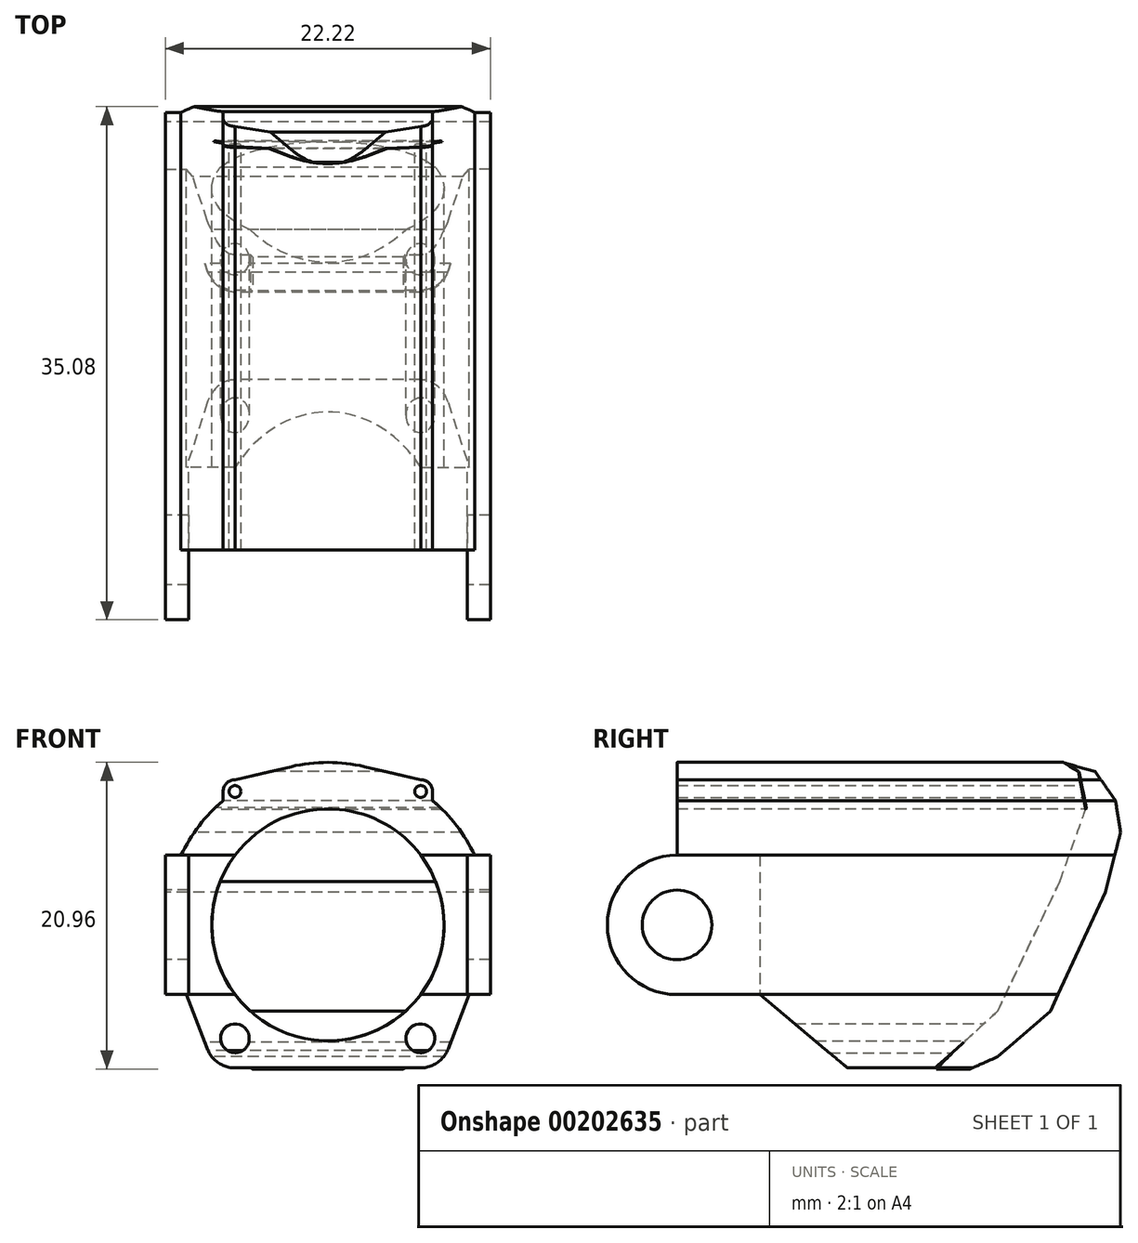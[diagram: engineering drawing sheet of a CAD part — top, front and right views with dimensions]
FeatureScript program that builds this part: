
annotation { "Feature Type Name" : "Feature", "Feature Type Description" : "" }
export const myFeature = defineFeature(function(context is Context, id is Id, definition is map)
    precondition{}
    {
        {
            var Q0;
            Q0=qCreatedBy(makeId("Front.planeOp"),FACE);
            var sketch = newSketch(context, id + "F0", { "sketchPlane" : qUnion([Q0])});
            skCircle(sketch, "E0", {"center": v(-21.38, 17.33) * mm, "radius": 7.94 * mm});
            skCircle(sketch, "E1", {"center": v(-21.38, 17.33) * mm, "radius": 9.53 * mm});
            skCircle(sketch, "E2", {"center": v(-21.38, 17.33) * mm, "radius": 11.11 * mm});
            skLineSegment(sketch, "E3", {"start": v(-33.5, 17.33) * mm, "end": v(-8.67, 17.33) * mm});
            skLineSegment(sketch, "E4", {"start": v(-21.38, 30.04) * mm, "end": v(-21.38, 4.75) * mm, "construction": true});
            skArc(sketch, "E5", {"start": v(-32.5, 17.33) * mm, "mid": v(-28.83, 10.36) * mm, "end": v(-21.38, 7.8) * mm});
            skArc(sketch, "E6", {"start": v(-21.38, 7.8) * mm, "mid": v(-13.93, 10.36) * mm, "end": v(-10.27, 17.33) * mm});
            skLineSegment(sketch, "E7", {"start": v(-31.3, 7.8) * mm, "end": v(-11.33, 7.78) * mm, "construction": true});
            skLineSegment(sketch, "E8", {"start": v(-31.32, 9.58) * mm, "end": v(-11.4, 9.58) * mm, "construction": true});
            skLineSegment(sketch, "E9", {"start": v(-27.73, 6.37) * mm, "end": v(-27.73, 30.2) * mm, "construction": true});
            skLineSegment(sketch, "E10", {"start": v(-15.06, 6.13) * mm, "end": v(-15.03, 30.29) * mm, "construction": true});
            skCircle(sketch, "E11", {"center": v(-15.06, 9.58) * mm, "radius": 1 * mm});
            skCircle(sketch, "E12", {"center": v(-15.06, 9.58) * mm, "radius": 2.03 * mm});
            skCircle(sketch, "E13", {"center": v(-27.73, 9.58) * mm, "radius": 1 * mm});
            skCircle(sketch, "E14", {"center": v(-27.73, 9.58) * mm, "radius": 2.03 * mm});
            skLineSegment(sketch, "E15", {"start": v(-31.83, 14.6) * mm, "end": v(-29.63, 8.85) * mm});
            skLineSegment(sketch, "E16", {"start": v(-10.98, 14.49) * mm, "end": v(-13.16, 8.85) * mm});
            skLineSegment(sketch, "E17", {"start": v(-27.73, 7.55) * mm, "end": v(-15.06, 7.55) * mm});
            skCircle(sketch, "E18", {"center": v(-15.04, 26.45) * mm, "radius": 0.4 * mm});
            skCircle(sketch, "E19", {"center": v(-27.73, 26.45) * mm, "radius": 0.4 * mm});
            skCircle(sketch, "E20", {"center": v(-27.73, 26.45) * mm, "radius": 0.81 * mm});
            skCircle(sketch, "E21", {"center": v(-15.04, 26.45) * mm, "radius": 0.81 * mm});
            skLineSegment(sketch, "E22", {"start": v(-27.73, 27.26) * mm, "end": v(-23.9, 28.15) * mm});
            skLineSegment(sketch, "E23", {"start": v(-15.03, 27.26) * mm, "end": v(-18.87, 28.15) * mm});
            skLineSegment(sketch, "E24", {"start": v(-15.54, 26.45) * mm, "end": v(-13.99, 26.45) * mm, "construction": true});
            skLineSegment(sketch, "E25", {"start": v(-27.17, 26.45) * mm, "end": v(-28.9, 26.45) * mm, "construction": true});
            skLineSegment(sketch, "E26", {"start": v(-28.54, 26.45) * mm, "end": v(-28.54, 25.82) * mm});
            skLineSegment(sketch, "E27", {"start": v(-14.22, 26.45) * mm, "end": v(-14.22, 25.83) * mm});
            skLineSegment(sketch, "E28", {"start": v(-13.44, 17.33) * mm, "end": v(-13.44, 28.69) * mm, "construction": true});
            skLineSegment(sketch, "E29", {"start": v(-29.32, 17.33) * mm, "end": v(-29.32, 27.77) * mm, "construction": true});
            skLineSegment(sketch, "E30.bottom", {"start": v(-13.44, 22.1) * mm, "end": v(-10.27, 22.1) * mm});
            skLineSegment(sketch, "E30.top", {"start": v(-13.44, 12.57) * mm, "end": v(-10.27, 12.57) * mm});
            skLineSegment(sketch, "E30.left", {"start": v(-13.44, 22.1) * mm, "end": v(-13.44, 12.57) * mm});
            skLineSegment(sketch, "E30.right", {"start": v(-10.27, 22.1) * mm, "end": v(-10.27, 12.57) * mm});
            skLineSegment(sketch, "E31.bottom", {"start": v(-29.32, 22.1) * mm, "end": v(-32.5, 22.1) * mm});
            skLineSegment(sketch, "E31.top", {"start": v(-29.32, 12.57) * mm, "end": v(-32.5, 12.57) * mm});
            skLineSegment(sketch, "E31.left", {"start": v(-29.32, 22.1) * mm, "end": v(-29.32, 12.57) * mm});
            skLineSegment(sketch, "E31.right", {"start": v(-32.5, 22.1) * mm, "end": v(-32.5, 12.57) * mm});
            skSolve(sketch);
        }
        {
            var Q0;
            {var subQ4=sQuery(id+"F0.wireOp",EDGE,"E30.bottom");var subQ6=sQuery(id+"F0.wireOp",EDGE,"E1");var subQ7=makeQuery(id+"F0.imprint","INTERSECT",VERTEX,{"derivedFrom":[subQ6,subQ4]});Q0=makeQuery(id+"F0.imprint","IMPRINT",FACE,{"disambiguationData":[TD([[makeQuery(id+"F0.imprint","IMPRINT",EDGE,{"disambiguationData":[TD([[subQ7,-1.0]])],"derivedFrom":subQ6}),-1.0]])]});}
            var Q1;
            {var subQ1=sQuery(id+"F0.wireOp",EDGE,"E30.bottom");var subQ9=sQuery(id+"F0.wireOp",EDGE,"E1");var subQ11=makeQuery(id+"F0.imprint","INTERSECT",VERTEX,{"derivedFrom":[subQ9,subQ1]});Q1=makeQuery(id+"F0.imprint","IMPRINT",FACE,{"disambiguationData":[TD([[makeQuery(id+"F0.imprint","IMPRINT",EDGE,{"disambiguationData":[TD([[subQ11,-1.0]])],"derivedFrom":subQ9}),1.0]])]});}
            var Q2;
            {var subQ0=sQuery(id+"F0.wireOp",EDGE,"E22");Q2=makeQuery(id+"F0.imprint","IMPRINT",FACE,{"disambiguationData":[TD([[makeQuery(id+"F0.imprint","IMPRINT",EDGE,{"derivedFrom":subQ0}),-1.0]])]});}
            var Q3;
            {var subQ0=sQuery(id+"F0.wireOp",EDGE,"E20");var subQ2=sQuery(id+"F0.wireOp",EDGE,"E2");var subQ3=makeQuery(id+"F0.imprint","INTERSECT",VERTEX,{"disambiguationData":[OD(0.0)],"derivedFrom":[subQ2,subQ0]});Q3=makeQuery(id+"F0.imprint","IMPRINT",FACE,{"disambiguationData":[TD([[makeQuery(id+"F0.imprint","IMPRINT",EDGE,{"disambiguationData":[TD([[subQ3,-1.0]])],"derivedFrom":subQ2}),-1.0]])]});}
            var Q4;
            {var subQ0=sQuery(id+"F0.wireOp",EDGE,"E20");var subQ1=sQuery(id+"F0.wireOp",EDGE,"E2");var subQ2=makeQuery(id+"F0.imprint","INTERSECT",VERTEX,{"disambiguationData":[OD(0.0)],"derivedFrom":[subQ1,subQ0]});Q4=makeQuery(id+"F0.imprint","IMPRINT",FACE,{"disambiguationData":[TD([[makeQuery(id+"F0.imprint","IMPRINT",EDGE,{"disambiguationData":[TD([[subQ2,-1.0]])],"derivedFrom":subQ1}),1.0]])]});}
            var Q5;
            {var subQ0=sQuery(id+"F0.wireOp",EDGE,"E26");Q5=makeQuery(id+"F0.imprint","IMPRINT",FACE,{"disambiguationData":[TD([[makeQuery(id+"F0.imprint","IMPRINT",EDGE,{"derivedFrom":subQ0}),1.0]])]});}
            var Q6;
            {var subQ0=sQuery(id+"F0.wireOp",EDGE,"E31.bottom");var subQ1=sQuery(id+"F0.wireOp",EDGE,"E1");var subQ2=makeQuery(id+"F0.imprint","INTERSECT",VERTEX,{"derivedFrom":[subQ1,subQ0]});Q6=makeQuery(id+"F0.imprint","IMPRINT",FACE,{"disambiguationData":[TD([[makeQuery(id+"F0.imprint","IMPRINT",EDGE,{"disambiguationData":[TD([[subQ2,-1.0]])],"derivedFrom":subQ1}),1.0]])]});}
            var Q7;
            {var subQ0=sQuery(id+"F0.wireOp",EDGE,"E31.bottom");var subQ1=sQuery(id+"F0.wireOp",EDGE,"E1");var subQ2=makeQuery(id+"F0.imprint","INTERSECT",VERTEX,{"derivedFrom":[subQ1,subQ0]});Q7=makeQuery(id+"F0.imprint","IMPRINT",FACE,{"disambiguationData":[TD([[makeQuery(id+"F0.imprint","IMPRINT",EDGE,{"disambiguationData":[TD([[subQ2,-1.0]])],"derivedFrom":subQ1}),-1.0]])]});}
            var Q8;
            {var subQ0=sQuery(id+"F0.wireOp",EDGE,"E31.right");var subQ3=sQuery(id+"F0.wireOp",EDGE,"E31.bottom");var subQ5=makeQuery(id+"F0.imprint","INTERSECT",VERTEX,{"derivedFrom":[subQ3,subQ0]});Q8=makeQuery(id+"F0.imprint","IMPRINT",FACE,{"disambiguationData":[TD([[makeQuery(id+"F0.imprint","IMPRINT",EDGE,{"disambiguationData":[TD([[subQ5,1.0]])],"derivedFrom":subQ3}),1.0]])]});}
            var Q9;
            {var subQ0=sQuery(id+"F0.wireOp",EDGE,"E3");var subQ1=sQuery(id+"F0.wireOp",EDGE,"E1");var subQ2=makeQuery(id+"F0.imprint","INTERSECT",VERTEX,{"disambiguationData":[OD(1.0)],"derivedFrom":[subQ1,subQ0]});Q9=makeQuery(id+"F0.imprint","IMPRINT",FACE,{"disambiguationData":[TD([[makeQuery(id+"F0.imprint","IMPRINT",EDGE,{"disambiguationData":[TD([[subQ2,-1.0]])],"derivedFrom":subQ1}),1.0]])]});}
            var Q10;
            {var subQ1=sQuery(id+"F0.wireOp",EDGE,"E3");var subQ4=sQuery(id+"F0.wireOp",EDGE,"E1");var subQ5=makeQuery(id+"F0.imprint","INTERSECT",VERTEX,{"disambiguationData":[OD(1.0)],"derivedFrom":[subQ4,subQ1]});Q10=makeQuery(id+"F0.imprint","IMPRINT",FACE,{"disambiguationData":[TD([[makeQuery(id+"F0.imprint","IMPRINT",EDGE,{"disambiguationData":[TD([[subQ5,-1.0]])],"derivedFrom":subQ4}),-1.0]])]});}
            var Q11;
            {var subQ0=sQuery(id+"F0.wireOp",EDGE,"E31.right");var subQ3=sQuery(id+"F0.wireOp",EDGE,"E31.top");var subQ5=makeQuery(id+"F0.imprint","INTERSECT",VERTEX,{"derivedFrom":[subQ3,subQ0]});Q11=makeQuery(id+"F0.imprint","IMPRINT",FACE,{"disambiguationData":[TD([[makeQuery(id+"F0.imprint","IMPRINT",EDGE,{"disambiguationData":[TD([[subQ5,1.0]])],"derivedFrom":subQ3}),-1.0]])]});}
            var Q12;
            {var subQ0=sQuery(id+"F0.wireOp",EDGE,"E5");var subQ5=sQuery(id+"F0.wireOp",EDGE,"E15");var subQ6=makeQuery(id+"F0.imprint","INTERSECT",VERTEX,{"derivedFrom":[subQ0,subQ5]});Q12=makeQuery(id+"F0.imprint","IMPRINT",FACE,{"disambiguationData":[TD([[makeQuery(id+"F0.imprint","IMPRINT",EDGE,{"disambiguationData":[TD([[subQ6,-1.0]])],"derivedFrom":subQ5}),-1.0]])]});}
            var Q13;
            {var subQ0=sQuery(id+"F0.wireOp",EDGE,"E15");var subQ1=sQuery(id+"F0.wireOp",EDGE,"E5");var subQ2=makeQuery(id+"F0.imprint","INTERSECT",VERTEX,{"derivedFrom":[subQ1,subQ0]});Q13=makeQuery(id+"F0.imprint","IMPRINT",FACE,{"disambiguationData":[TD([[makeQuery(id+"F0.imprint","IMPRINT",EDGE,{"disambiguationData":[TD([[subQ2,-1.0]])],"derivedFrom":subQ1}),-1.0]])]});}
            var Q14;
            {var subQ1=sQuery(id+"F0.wireOp",EDGE,"E31.top");var subQ3=sQuery(id+"F0.wireOp",EDGE,"E1");var subQ4=makeQuery(id+"F0.imprint","INTERSECT",VERTEX,{"derivedFrom":[subQ3,subQ1]});Q14=makeQuery(id+"F0.imprint","IMPRINT",FACE,{"disambiguationData":[TD([[makeQuery(id+"F0.imprint","IMPRINT",EDGE,{"disambiguationData":[TD([[subQ4,-1.0]])],"derivedFrom":subQ3}),1.0]])]});}
            var Q15;
            {var subQ1=sQuery(id+"F0.wireOp",EDGE,"E2");var subQ5=sQuery(id+"F0.wireOp",EDGE,"E15");var subQ6=makeQuery(id+"F0.imprint","INTERSECT",VERTEX,{"derivedFrom":[subQ1,subQ5]});Q15=makeQuery(id+"F0.imprint","IMPRINT",FACE,{"disambiguationData":[TD([[makeQuery(id+"F0.imprint","IMPRINT",EDGE,{"disambiguationData":[TD([[subQ6,-1.0]])],"derivedFrom":subQ1}),1.0]])]});}
            var Q16;
            {var subQ0=sQuery(id+"F0.wireOp",EDGE,"E31.top");var subQ1=sQuery(id+"F0.wireOp",EDGE,"E1");var subQ2=makeQuery(id+"F0.imprint","INTERSECT",VERTEX,{"derivedFrom":[subQ1,subQ0]});Q16=makeQuery(id+"F0.imprint","IMPRINT",FACE,{"disambiguationData":[TD([[makeQuery(id+"F0.imprint","IMPRINT",EDGE,{"disambiguationData":[TD([[subQ2,-1.0]])],"derivedFrom":subQ1}),-1.0]])]});}
            var Q17;
            {var subQ0=sQuery(id+"F0.wireOp",EDGE,"E14");var subQ1=sQuery(id+"F0.wireOp",EDGE,"E1");var subQ2=makeQuery(id+"F0.imprint","INTERSECT",VERTEX,{"disambiguationData":[OD(0.0)],"derivedFrom":[subQ1,subQ0]});Q17=makeQuery(id+"F0.imprint","IMPRINT",FACE,{"disambiguationData":[TD([[makeQuery(id+"F0.imprint","IMPRINT",EDGE,{"disambiguationData":[TD([[subQ2,-1.0]])],"derivedFrom":subQ1}),1.0]])]});}
            var Q18;
            {var subQ0=sQuery(id+"F0.wireOp",EDGE,"E14");var subQ1=sQuery(id+"F0.wireOp",EDGE,"E1");var subQ2=makeQuery(id+"F0.imprint","INTERSECT",VERTEX,{"disambiguationData":[OD(0.0)],"derivedFrom":[subQ1,subQ0]});Q18=makeQuery(id+"F0.imprint","IMPRINT",FACE,{"disambiguationData":[TD([[makeQuery(id+"F0.imprint","IMPRINT",EDGE,{"disambiguationData":[TD([[subQ2,-1.0]])],"derivedFrom":subQ1}),-1.0]])]});}
            var Q19;
            {var subQ4=sQuery(id+"F0.wireOp",EDGE,"E14");var subQ7=sQuery(id+"F0.wireOp",EDGE,"E2");var subQ9=makeQuery(id+"F0.imprint","INTERSECT",VERTEX,{"disambiguationData":[OD(0.0)],"derivedFrom":[subQ7,subQ4]});Q19=makeQuery(id+"F0.imprint","IMPRINT",FACE,{"disambiguationData":[TD([[makeQuery(id+"F0.imprint","IMPRINT",EDGE,{"disambiguationData":[TD([[subQ9,-1.0]])],"derivedFrom":subQ7}),1.0]])]});}
            var Q20;
            {var subQ0=sQuery(id+"F0.wireOp",EDGE,"E13");var subQ1=sQuery(id+"F0.wireOp",EDGE,"E1");var subQ2=makeQuery(id+"F0.imprint","INTERSECT",VERTEX,{"disambiguationData":[OD(1.0)],"derivedFrom":[subQ1,subQ0]});Q20=makeQuery(id+"F0.imprint","IMPRINT",FACE,{"disambiguationData":[TD([[makeQuery(id+"F0.imprint","IMPRINT",EDGE,{"disambiguationData":[TD([[subQ2,-1.0]])],"derivedFrom":subQ1}),-1.0]])]});}
            var Q21;
            {var subQ0=sQuery(id+"F0.wireOp",EDGE,"E14");var subQ1=sQuery(id+"F0.wireOp",EDGE,"E2");var subQ2=makeQuery(id+"F0.imprint","INTERSECT",VERTEX,{"disambiguationData":[OD(0.0)],"derivedFrom":[subQ1,subQ0]});Q21=makeQuery(id+"F0.imprint","IMPRINT",FACE,{"disambiguationData":[TD([[makeQuery(id+"F0.imprint","IMPRINT",EDGE,{"disambiguationData":[TD([[subQ2,-1.0]])],"derivedFrom":subQ1}),-1.0]])]});}
            var Q22;
            {var subQ0=sQuery(id+"F0.wireOp",EDGE,"E15");var subQ1=sQuery(id+"F0.wireOp",EDGE,"E2");var subQ2=makeQuery(id+"F0.imprint","INTERSECT",VERTEX,{"derivedFrom":[subQ1,subQ0]});Q22=makeQuery(id+"F0.imprint","IMPRINT",FACE,{"disambiguationData":[TD([[makeQuery(id+"F0.imprint","IMPRINT",EDGE,{"disambiguationData":[TD([[subQ2,-1.0]])],"derivedFrom":subQ1}),-1.0]])]});}
            var Q23;
            {var subQ1=sQuery(id+"F0.wireOp",EDGE,"E1");var subQ3=sQuery(id+"F0.wireOp",EDGE,"E14");var subQ4=makeQuery(id+"F0.imprint","INTERSECT",VERTEX,{"disambiguationData":[OD(1.0)],"derivedFrom":[subQ1,subQ3]});Q23=makeQuery(id+"F0.imprint","IMPRINT",FACE,{"disambiguationData":[TD([[makeQuery(id+"F0.imprint","IMPRINT",EDGE,{"disambiguationData":[TD([[subQ4,1.0]])],"derivedFrom":subQ3}),-1.0]])]});}
            var Q24;
            {var subQ7=sQuery(id+"F0.wireOp",EDGE,"E17");var subQ8=sQuery(id+"F0.wireOp",EDGE,"E2");var subQ11=makeQuery(id+"F0.imprint","INTERSECT",VERTEX,{"disambiguationData":[OD(0.0)],"derivedFrom":[subQ8,subQ7]});Q24=makeQuery(id+"F0.imprint","IMPRINT",FACE,{"disambiguationData":[TD([[makeQuery(id+"F0.imprint","IMPRINT",EDGE,{"disambiguationData":[TD([[subQ11,1.0]])],"derivedFrom":subQ8}),1.0]])]});}
            var Q25;
            {var subQ0=sQuery(id+"F0.wireOp",EDGE,"E17");var subQ1=sQuery(id+"F0.wireOp",EDGE,"E2");var subQ2=makeQuery(id+"F0.imprint","INTERSECT",VERTEX,{"disambiguationData":[OD(0.0)],"derivedFrom":[subQ1,subQ0]});Q25=makeQuery(id+"F0.imprint","IMPRINT",FACE,{"disambiguationData":[TD([[makeQuery(id+"F0.imprint","IMPRINT",EDGE,{"disambiguationData":[TD([[subQ2,1.0]])],"derivedFrom":subQ1}),-1.0]])]});}
            var Q26;
            {var subQ1=sQuery(id+"F0.wireOp",EDGE,"E1");var subQ3=sQuery(id+"F0.wireOp",EDGE,"E12");var subQ4=makeQuery(id+"F0.imprint","INTERSECT",VERTEX,{"disambiguationData":[OD(0.0)],"derivedFrom":[subQ1,subQ3]});Q26=makeQuery(id+"F0.imprint","IMPRINT",FACE,{"disambiguationData":[TD([[makeQuery(id+"F0.imprint","IMPRINT",EDGE,{"disambiguationData":[TD([[subQ4,-1.0]])],"derivedFrom":subQ3}),-1.0]])]});}
            var Q27;
            {var subQ0=sQuery(id+"F0.wireOp",EDGE,"E12");var subQ1=sQuery(id+"F0.wireOp",EDGE,"E1");var subQ2=makeQuery(id+"F0.imprint","INTERSECT",VERTEX,{"disambiguationData":[OD(0.0)],"derivedFrom":[subQ1,subQ0]});Q27=makeQuery(id+"F0.imprint","IMPRINT",FACE,{"disambiguationData":[TD([[makeQuery(id+"F0.imprint","IMPRINT",EDGE,{"disambiguationData":[TD([[subQ2,-1.0]])],"derivedFrom":subQ1}),1.0]])]});}
            var Q28;
            {var subQ0=sQuery(id+"F0.wireOp",EDGE,"E12");var subQ1=sQuery(id+"F0.wireOp",EDGE,"E1");var subQ2=makeQuery(id+"F0.imprint","INTERSECT",VERTEX,{"disambiguationData":[OD(0.0)],"derivedFrom":[subQ1,subQ0]});Q28=makeQuery(id+"F0.imprint","IMPRINT",FACE,{"disambiguationData":[TD([[makeQuery(id+"F0.imprint","IMPRINT",EDGE,{"disambiguationData":[TD([[subQ2,-1.0]])],"derivedFrom":subQ1}),-1.0]])]});}
            var Q29;
            {var subQ4=sQuery(id+"F0.wireOp",EDGE,"E12");var subQ7=sQuery(id+"F0.wireOp",EDGE,"E2");var subQ8=makeQuery(id+"F0.imprint","INTERSECT",VERTEX,{"disambiguationData":[OD(0.0)],"derivedFrom":[subQ7,subQ4]});Q29=makeQuery(id+"F0.imprint","IMPRINT",FACE,{"disambiguationData":[TD([[makeQuery(id+"F0.imprint","IMPRINT",EDGE,{"disambiguationData":[TD([[subQ8,-1.0]])],"derivedFrom":subQ7}),1.0]])]});}
            var Q30;
            {var subQ0=sQuery(id+"F0.wireOp",EDGE,"E17");var subQ1=sQuery(id+"F0.wireOp",EDGE,"E2");var subQ2=makeQuery(id+"F0.imprint","INTERSECT",VERTEX,{"disambiguationData":[OD(1.0)],"derivedFrom":[subQ1,subQ0]});Q30=makeQuery(id+"F0.imprint","IMPRINT",FACE,{"disambiguationData":[TD([[makeQuery(id+"F0.imprint","IMPRINT",EDGE,{"disambiguationData":[TD([[subQ2,-1.0]])],"derivedFrom":subQ1}),-1.0]])]});}
            var Q31;
            {var subQ0=sQuery(id+"F0.wireOp",EDGE,"E12");var subQ1=sQuery(id+"F0.wireOp",EDGE,"E2");var subQ2=makeQuery(id+"F0.imprint","INTERSECT",VERTEX,{"disambiguationData":[OD(0.0)],"derivedFrom":[subQ1,subQ0]});Q31=makeQuery(id+"F0.imprint","IMPRINT",FACE,{"disambiguationData":[TD([[makeQuery(id+"F0.imprint","IMPRINT",EDGE,{"disambiguationData":[TD([[subQ2,-1.0]])],"derivedFrom":subQ1}),-1.0]])]});}
            var Q32;
            {var subQ0=sQuery(id+"F0.wireOp",EDGE,"E16");var subQ1=sQuery(id+"F0.wireOp",EDGE,"E2");var subQ2=makeQuery(id+"F0.imprint","INTERSECT",VERTEX,{"derivedFrom":[subQ1,subQ0]});Q32=makeQuery(id+"F0.imprint","IMPRINT",FACE,{"disambiguationData":[TD([[makeQuery(id+"F0.imprint","IMPRINT",EDGE,{"disambiguationData":[TD([[subQ2,1.0]])],"derivedFrom":subQ1}),-1.0]])]});}
            var Q33;
            {var subQ1=sQuery(id+"F0.wireOp",EDGE,"E2");var subQ5=sQuery(id+"F0.wireOp",EDGE,"E16");var subQ6=makeQuery(id+"F0.imprint","INTERSECT",VERTEX,{"derivedFrom":[subQ1,subQ5]});Q33=makeQuery(id+"F0.imprint","IMPRINT",FACE,{"disambiguationData":[TD([[makeQuery(id+"F0.imprint","IMPRINT",EDGE,{"disambiguationData":[TD([[subQ6,1.0]])],"derivedFrom":subQ1}),1.0]])]});}
            var Q34;
            {var subQ0=sQuery(id+"F0.wireOp",EDGE,"E12");var subQ1=sQuery(id+"F0.wireOp",EDGE,"E1");var subQ2=makeQuery(id+"F0.imprint","INTERSECT",VERTEX,{"disambiguationData":[OD(1.0)],"derivedFrom":[subQ1,subQ0]});Q34=makeQuery(id+"F0.imprint","IMPRINT",FACE,{"disambiguationData":[TD([[makeQuery(id+"F0.imprint","IMPRINT",EDGE,{"disambiguationData":[TD([[subQ2,-1.0]])],"derivedFrom":subQ1}),-1.0]])]});}
            var Q35;
            {var subQ0=sQuery(id+"F0.wireOp",EDGE,"E11");var subQ1=sQuery(id+"F0.wireOp",EDGE,"E1");var subQ2=makeQuery(id+"F0.imprint","INTERSECT",VERTEX,{"disambiguationData":[OD(1.0)],"derivedFrom":[subQ1,subQ0]});Q35=makeQuery(id+"F0.imprint","IMPRINT",FACE,{"disambiguationData":[TD([[makeQuery(id+"F0.imprint","IMPRINT",EDGE,{"disambiguationData":[TD([[subQ2,-1.0]])],"derivedFrom":subQ1}),-1.0]])]});}
            var Q36;
            {var subQ0=sQuery(id+"F0.wireOp",EDGE,"E3");var subQ1=sQuery(id+"F0.wireOp",EDGE,"E1");var subQ2=makeQuery(id+"F0.imprint","INTERSECT",VERTEX,{"disambiguationData":[OD(0.0)],"derivedFrom":[subQ1,subQ0]});Q36=makeQuery(id+"F0.imprint","IMPRINT",FACE,{"disambiguationData":[TD([[makeQuery(id+"F0.imprint","IMPRINT",EDGE,{"disambiguationData":[TD([[subQ2,1.0]])],"derivedFrom":subQ1}),1.0]])]});}
            var Q37;
            {var subQ4=sQuery(id+"F0.wireOp",EDGE,"E3");var subQ6=sQuery(id+"F0.wireOp",EDGE,"E1");var subQ7=makeQuery(id+"F0.imprint","INTERSECT",VERTEX,{"disambiguationData":[OD(0.0)],"derivedFrom":[subQ6,subQ4]});Q37=makeQuery(id+"F0.imprint","IMPRINT",FACE,{"disambiguationData":[TD([[makeQuery(id+"F0.imprint","IMPRINT",EDGE,{"disambiguationData":[TD([[subQ7,1.0]])],"derivedFrom":subQ6}),-1.0]])]});}
            var Q38;
            {var subQ0=sQuery(id+"F0.wireOp",EDGE,"E16");var subQ1=sQuery(id+"F0.wireOp",EDGE,"E6");var subQ2=makeQuery(id+"F0.imprint","INTERSECT",VERTEX,{"derivedFrom":[subQ1,subQ0]});Q38=makeQuery(id+"F0.imprint","IMPRINT",FACE,{"disambiguationData":[TD([[makeQuery(id+"F0.imprint","IMPRINT",EDGE,{"disambiguationData":[TD([[subQ2,1.0]])],"derivedFrom":subQ1}),-1.0]])]});}
            var Q39;
            {var subQ0=sQuery(id+"F0.wireOp",EDGE,"E6");var subQ5=sQuery(id+"F0.wireOp",EDGE,"E16");var subQ6=makeQuery(id+"F0.imprint","INTERSECT",VERTEX,{"derivedFrom":[subQ0,subQ5]});Q39=makeQuery(id+"F0.imprint","IMPRINT",FACE,{"disambiguationData":[TD([[makeQuery(id+"F0.imprint","IMPRINT",EDGE,{"disambiguationData":[TD([[subQ6,-1.0]])],"derivedFrom":subQ5}),1.0]])]});}
            var Q40;
            {var subQ0=sQuery(id+"F0.wireOp",EDGE,"E30.right");var subQ3=sQuery(id+"F0.wireOp",EDGE,"E30.top");var subQ5=makeQuery(id+"F0.imprint","INTERSECT",VERTEX,{"derivedFrom":[subQ3,subQ0]});Q40=makeQuery(id+"F0.imprint","IMPRINT",FACE,{"disambiguationData":[TD([[makeQuery(id+"F0.imprint","IMPRINT",EDGE,{"disambiguationData":[TD([[subQ5,1.0]])],"derivedFrom":subQ3}),1.0]])]});}
            var Q41;
            {var subQ0=sQuery(id+"F0.wireOp",EDGE,"E30.right");var subQ3=sQuery(id+"F0.wireOp",EDGE,"E30.bottom");var subQ5=makeQuery(id+"F0.imprint","INTERSECT",VERTEX,{"derivedFrom":[subQ3,subQ0]});Q41=makeQuery(id+"F0.imprint","IMPRINT",FACE,{"disambiguationData":[TD([[makeQuery(id+"F0.imprint","IMPRINT",EDGE,{"disambiguationData":[TD([[subQ5,1.0]])],"derivedFrom":subQ3}),-1.0]])]});}
            var Q42;
            {var subQ0=sQuery(id+"F0.wireOp",EDGE,"E30.bottom");var subQ1=sQuery(id+"F0.wireOp",EDGE,"E1");var subQ2=makeQuery(id+"F0.imprint","INTERSECT",VERTEX,{"derivedFrom":[subQ1,subQ0]});Q42=makeQuery(id+"F0.imprint","IMPRINT",FACE,{"disambiguationData":[TD([[makeQuery(id+"F0.imprint","IMPRINT",EDGE,{"disambiguationData":[TD([[subQ2,1.0]])],"derivedFrom":subQ1}),-1.0]])]});}
            var Q43;
            {var subQ0=sQuery(id+"F0.wireOp",EDGE,"E30.bottom");var subQ1=sQuery(id+"F0.wireOp",EDGE,"E1");var subQ2=makeQuery(id+"F0.imprint","INTERSECT",VERTEX,{"derivedFrom":[subQ1,subQ0]});Q43=makeQuery(id+"F0.imprint","IMPRINT",FACE,{"disambiguationData":[TD([[makeQuery(id+"F0.imprint","IMPRINT",EDGE,{"disambiguationData":[TD([[subQ2,1.0]])],"derivedFrom":subQ1}),1.0]])]});}
            var Q44;
            {var subQ0=sQuery(id+"F0.wireOp",EDGE,"E23");Q44=makeQuery(id+"F0.imprint","IMPRINT",FACE,{"disambiguationData":[TD([[makeQuery(id+"F0.imprint","IMPRINT",EDGE,{"derivedFrom":subQ0}),1.0]])]});}
            var Q45;
            {var subQ0=sQuery(id+"F0.wireOp",EDGE,"E21");var subQ3=sQuery(id+"F0.wireOp",EDGE,"E2");var subQ4=makeQuery(id+"F0.imprint","INTERSECT",VERTEX,{"disambiguationData":[OD(0.0)],"derivedFrom":[subQ3,subQ0]});Q45=makeQuery(id+"F0.imprint","IMPRINT",FACE,{"disambiguationData":[TD([[makeQuery(id+"F0.imprint","IMPRINT",EDGE,{"disambiguationData":[TD([[subQ4,-1.0]])],"derivedFrom":subQ3}),-1.0]])]});}
            var Q46;
            {var subQ0=sQuery(id+"F0.wireOp",EDGE,"E21");var subQ1=sQuery(id+"F0.wireOp",EDGE,"E2");var subQ2=makeQuery(id+"F0.imprint","INTERSECT",VERTEX,{"disambiguationData":[OD(0.0)],"derivedFrom":[subQ1,subQ0]});Q46=makeQuery(id+"F0.imprint","IMPRINT",FACE,{"disambiguationData":[TD([[makeQuery(id+"F0.imprint","IMPRINT",EDGE,{"disambiguationData":[TD([[subQ2,-1.0]])],"derivedFrom":subQ1}),1.0]])]});}
            var Q47;
            {var subQ0=sQuery(id+"F0.wireOp",EDGE,"E27");Q47=makeQuery(id+"F0.imprint","IMPRINT",FACE,{"disambiguationData":[TD([[makeQuery(id+"F0.imprint","IMPRINT",EDGE,{"derivedFrom":subQ0}),-1.0]])]});}
            extrude(context, id + "F1", {"entities" : qUnion([Q0, Q1, Q2, Q3, Q4, Q5, Q6, Q7, Q8, Q9, Q10, Q11, Q12, Q13, Q14, Q15, Q16, Q17, Q18, Q19, Q20, Q21, Q22, Q23, Q24, Q25, Q26, Q27, Q28, Q29, Q30, Q31, Q32, Q33, Q34, Q35, Q36, Q37, Q38, Q39, Q40, Q41, Q42, Q43, Q44, Q45, Q46, Q47]), "depth" : 38.1 * mm});
        }
        {
            var Q0;
            Q0=makeQuery(id+"F1.opExtrude","SWEPT_FACE",FACE,{"disambiguationData":[OSD([sQuery(id+"F0.wireOp",EDGE,"E31.right")])]});
            var sketch = newSketch(context, id + "F2", { "sketchPlane" : qUnion([Q0])});
            skLineSegment(sketch, "E32", {"start": v(-3.09, 17.33) * mm, "end": v(40.51, 17.33) * mm, "construction": true});
            skPoint(sketch, "E32.startSnap0", {"position": v(0, 17.33) * mm});
            skCircle(sketch, "E33", {"center": v(19.05, 17.33) * mm, "radius": 11.18 * mm});
            skLineSegment(sketch, "E34", {"start": v(19.05, 3.38) * mm, "end": v(19.05, 35.9) * mm});
            skLineSegment(sketch, "E35", {"start": v(19.05, 35.9) * mm, "end": v(-4.68, 35.9) * mm});
            skLineSegment(sketch, "E36", {"start": v(-4.68, 35.9) * mm, "end": v(-4.68, 3.38) * mm});
            skLineSegment(sketch, "E37", {"start": v(-4.68, 3.38) * mm, "end": v(19.05, 3.38) * mm});
            skLineSegment(sketch, "E38", {"start": v(19.05, 28.85) * mm, "end": v(9.85, 28.85) * mm});
            skLineSegment(sketch, "E39", {"start": v(9.85, 28.85) * mm, "end": v(5.07, 28.85) * mm});
            skLineSegment(sketch, "E40", {"start": v(5.07, 28.85) * mm, "end": v(3.41, 27.8) * mm});
            skLineSegment(sketch, "E41", {"start": v(3.41, 27.8) * mm, "end": v(2.91, 25.23) * mm});
            skLineSegment(sketch, "E42", {"start": v(2.91, 25.23) * mm, "end": v(4.68, 20.3) * mm});
            skLineSegment(sketch, "E43", {"start": v(4.68, 20.3) * mm, "end": v(8.96, 11.36) * mm});
            skLineSegment(sketch, "E44", {"start": v(8.96, 11.36) * mm, "end": v(13.76, 7.06) * mm});
            skLineSegment(sketch, "E45", {"start": v(13.76, 7.06) * mm, "end": v(19.05, 5.87) * mm});
            skSolve(sketch);
        }
        {
            var Q0;
            {var subQ10=sQuery(id+"F2.wireOp",EDGE,"E35");Q0=makeQuery(id+"F2.imprint","IMPRINT",FACE,{"disambiguationData":[TD([[makeQuery(id+"F2.imprint","IMPRINT",EDGE,{"derivedFrom":subQ10}),1.0]])]});}
            var Q1;
            {var subQ0=sQuery(id+"F0.wireOp",EDGE,"E31.right");var subQ1=makeQuery(id+"F1.opExtrude","CAP_EDGE",EDGE,{"disambiguationData":[OSD([subQ0])],"isStart":true});Q1=makeQuery(id+"F2.imprint","IMPRINT",FACE,{"disambiguationData":[TD([[makeQuery(id+"F2.imprint","IMPRINT",EDGE,{"derivedFrom":subQ1}),1.0]])]});}
            extrude(context, id + "F3", {"entities" : qUnion([Q0, Q1]), "operationType" : NewBodyOperationType.REMOVE, "oppositeDirection" : true, "depth" : 25.4 * mm});
        }
        {
            var Q0;
            Q0=makeQuery(id+"F1.opExtrude","SWEPT_FACE",FACE,{"disambiguationData":[OSD([sQuery(id+"F0.wireOp",EDGE,"E31.right")])]});
            var sketch = newSketch(context, id + "F4", { "sketchPlane" : qUnion([Q0])});
            skLineSegment(sketch, "E46", {"start": v(4.04, 22.1) * mm, "end": v(2.87, 25.35) * mm});
            skLineSegment(sketch, "E47", {"start": v(2.87, 25.35) * mm, "end": v(3.38, 27.82) * mm});
            skLineSegment(sketch, "E48", {"start": v(3.38, 27.82) * mm, "end": v(4.34, 28.4) * mm});
            skLineSegment(sketch, "E49", {"start": v(4.34, 28.4) * mm, "end": v(2.26, 27.82) * mm});
            skLineSegment(sketch, "E50", {"start": v(2.26, 27.82) * mm, "end": v(0.87, 25.82) * mm});
            skLineSegment(sketch, "E51", {"start": v(0.87, 25.82) * mm, "end": v(0.53, 23.66) * mm});
            skLineSegment(sketch, "E52", {"start": v(0.53, 23.66) * mm, "end": v(1.57, 19.58) * mm});
            skLineSegment(sketch, "E53", {"start": v(1.57, 19.58) * mm, "end": v(5.3, 11.45) * mm});
            skLineSegment(sketch, "E54", {"start": v(5.3, 11.45) * mm, "end": v(8.92, 8.33) * mm});
            skLineSegment(sketch, "E55", {"start": v(8.92, 8.33) * mm, "end": v(10.81, 7.48) * mm});
            skLineSegment(sketch, "E56", {"start": v(10.81, 7.48) * mm, "end": v(13.12, 7.48) * mm});
            skLineSegment(sketch, "E57", {"start": v(13.12, 7.48) * mm, "end": v(11.85, 8.75) * mm});
            skLineSegment(sketch, "E58", {"start": v(11.85, 8.75) * mm, "end": v(8.92, 11.45) * mm});
            skLineSegment(sketch, "E59", {"start": v(8.92, 11.45) * mm, "end": v(4.68, 20.3) * mm});
            skLineSegment(sketch, "E60", {"start": v(4.68, 20.3) * mm, "end": v(4.04, 22.1) * mm});
            skSolve(sketch);
        }
        {
            var Q0;
            Q0 = qSketchRegion(id + "F4", true);
            var Q1;
            Q1=makeQuery(id+"F1.opExtrude","SWEPT_FACE",FACE,{"disambiguationData":[OSD([sQuery(id+"F0.wireOp",EDGE,"E30.right")])]});
            extrude(context, id + "F5", {"entities" : qUnion([Q0]), "operationType" : NewBodyOperationType.ADD, "endBound" : BoundingType.UP_TO_SURFACE, "oppositeDirection" : true, "endBoundEntityFace" : qUnion([Q1]), "depth" : 25.4 * mm});
        }
        {
            var Q0;
            Q0=makeQuery(id+"F1.opExtrude","CAP_FACE",FACE,{"disambiguationData":[OSD([sQuery(id+"F0.wireOp",EDGE,"E0"),sQuery(id+"F0.wireOp",EDGE,"E2"),sQuery(id+"F0.wireOp",EDGE,"E11"),sQuery(id+"F0.wireOp",EDGE,"E12"),sQuery(id+"F0.wireOp",EDGE,"E13"),sQuery(id+"F0.wireOp",EDGE,"E14"),sQuery(id+"F0.wireOp",EDGE,"E15"),sQuery(id+"F0.wireOp",EDGE,"E16"),sQuery(id+"F0.wireOp",EDGE,"E17"),sQuery(id+"F0.wireOp",EDGE,"E18"),sQuery(id+"F0.wireOp",EDGE,"E19"),sQuery(id+"F0.wireOp",EDGE,"E20"),sQuery(id+"F0.wireOp",EDGE,"E21"),sQuery(id+"F0.wireOp",EDGE,"E22"),sQuery(id+"F0.wireOp",EDGE,"E23"),sQuery(id+"F0.wireOp",EDGE,"E26"),sQuery(id+"F0.wireOp",EDGE,"E27"),sQuery(id+"F0.wireOp",EDGE,"E30.bottom"),sQuery(id+"F0.wireOp",EDGE,"E30.top"),sQuery(id+"F0.wireOp",EDGE,"E30.right"),sQuery(id+"F0.wireOp",EDGE,"E31.bottom"),sQuery(id+"F0.wireOp",EDGE,"E31.top"),sQuery(id+"F0.wireOp",EDGE,"E31.right")])],"isStart":false});
            var sketch = newSketch(context, id + "F6", { "sketchPlane" : qUnion([Q0])});
            skArc(sketch, "E61", {"start": v(-11.34, 12.57) * mm, "mid": v(-21.38, 28.44) * mm, "end": v(-31.42, 12.57) * mm});
            skLineSegment(sketch, "E62", {"start": v(-33.68, 22.1) * mm, "end": v(-31.42, 22.1) * mm});
            skLineSegment(sketch, "E63", {"start": v(-31.42, 22.1) * mm, "end": v(-28.54, 25.82) * mm});
            skLineSegment(sketch, "E64", {"start": v(-28.54, 25.82) * mm, "end": v(-28.54, 26.45) * mm});
            skLineSegment(sketch, "E65", {"start": v(-28.54, 26.45) * mm, "end": v(-27.73, 27.26) * mm});
            skLineSegment(sketch, "E66", {"start": v(-27.73, 27.26) * mm, "end": v(-23.9, 28.15) * mm});
            skLineSegment(sketch, "E67", {"start": v(-8.91, 22.1) * mm, "end": v(-11.34, 22.1) * mm});
            skLineSegment(sketch, "E68", {"start": v(-11.34, 22.1) * mm, "end": v(-14.22, 25.83) * mm});
            skLineSegment(sketch, "E69", {"start": v(-14.22, 25.83) * mm, "end": v(-14.22, 26.45) * mm});
            skLineSegment(sketch, "E70", {"start": v(-14.22, 26.45) * mm, "end": v(-15.03, 27.26) * mm});
            skLineSegment(sketch, "E71", {"start": v(-15.03, 27.26) * mm, "end": v(-18.87, 28.15) * mm});
            skCircle(sketch, "E72", {"center": v(-27.73, 26.45) * mm, "radius": 0.81 * mm});
            skCircle(sketch, "E73", {"center": v(-15.04, 26.45) * mm, "radius": 0.81 * mm});
            skLineSegment(sketch, "E74", {"start": v(-10.27, 12.57) * mm, "end": v(-11.72, 12.57) * mm});
            skLineSegment(sketch, "E75", {"start": v(-11.72, 12.57) * mm, "end": v(-13.16, 8.85) * mm});
            skLineSegment(sketch, "E76", {"start": v(-13.16, 8.85) * mm, "end": v(-15.06, 7.55) * mm});
            skLineSegment(sketch, "E77", {"start": v(-15.06, 7.55) * mm, "end": v(-27.73, 7.55) * mm});
            skLineSegment(sketch, "E78", {"start": v(-27.73, 7.55) * mm, "end": v(-29.63, 8.85) * mm});
            skLineSegment(sketch, "E79", {"start": v(-29.63, 8.85) * mm, "end": v(-31.05, 12.57) * mm});
            skLineSegment(sketch, "E80", {"start": v(-31.05, 12.57) * mm, "end": v(-34.02, 12.57) * mm});
            skLineSegment(sketch, "E81", {"start": v(-32.5, 29.5) * mm, "end": v(-32.5, 5.4) * mm});
            skLineSegment(sketch, "E82", {"start": v(-10.27, 29.32) * mm, "end": v(-10.27, 5.9) * mm});
            skCircle(sketch, "E83", {"center": v(-15.06, 9.58) * mm, "radius": 2.03 * mm});
            skCircle(sketch, "E84", {"center": v(-27.73, 9.58) * mm, "radius": 2.03 * mm});
            skLineSegment(sketch, "E85", {"start": v(-32.5, 29.5) * mm, "end": v(-10.27, 29.5) * mm});
            skLineSegment(sketch, "E86", {"start": v(-10.27, 29.5) * mm, "end": v(-10.27, 29.32) * mm});
            skArc(sketch, "E87.trimOffspring", {"start": v(-30.38, 10.8) * mm, "mid": v(-21.41, 6.22) * mm, "end": v(-12.42, 10.75) * mm});
            skLineSegment(sketch, "E88", {"start": v(-32.5, 5.4) * mm, "end": v(-10.27, 5.4) * mm});
            skLineSegment(sketch, "E89", {"start": v(-10.27, 5.4) * mm, "end": v(-10.27, 5.9) * mm});
            skSolve(sketch);
        }
        {
            var Q0;
            {var subQ0=sQuery(id+"F6.wireOp",EDGE,"E87.trimOffspring");var subQ1=sQuery(id+"F6.wireOp",EDGE,"E77");var subQ2=makeQuery(id+"F6.imprint","INTERSECT",VERTEX,{"disambiguationData":[OD(0.0)],"derivedFrom":[subQ1,subQ0]});Q0=makeQuery(id+"F6.imprint","IMPRINT",FACE,{"disambiguationData":[TD([[makeQuery(id+"F6.imprint","IMPRINT",EDGE,{"disambiguationData":[TD([[subQ2,-1.0]])],"derivedFrom":subQ1}),-1.0]])]});}
            var Q1;
            {var subQ26=sQuery(id+"F6.wireOp",EDGE,"E88");Q1=makeQuery(id+"F6.imprint","IMPRINT",FACE,{"disambiguationData":[TD([[makeQuery(id+"F6.imprint","IMPRINT",EDGE,{"derivedFrom":subQ26}),1.0]])]});}
            var Q2;
            {var subQ3=sQuery(id+"F6.wireOp",EDGE,"E64");Q2=makeQuery(id+"F6.imprint","IMPRINT",FACE,{"disambiguationData":[TD([[makeQuery(id+"F6.imprint","IMPRINT",EDGE,{"derivedFrom":subQ3}),-1.0]])]});}
            extrude(context, id + "F7", {"entities" : qUnion([Q0, Q1, Q2]), "operationType" : NewBodyOperationType.REMOVE, "endBound" : BoundingType.THROUGH_ALL, "oppositeDirection" : true, "depth" : 25.4 * mm});
        }
        {
            var Q0;
            Q0=makeQuery(id+"F5.boolean.opBoolean","MERGE",FACE,{"derivedFrom":[makeQuery(id+"F1.opExtrude","SWEPT_FACE",FACE,{"disambiguationData":[OSD([sQuery(id+"F0.wireOp",EDGE,"E31.right")])]}),makeQuery(id+"F5.opExtrude","CAP_FACE",FACE,{"disambiguationData":[OSD([sQuery(id+"F4.wireOp",EDGE,"E46"),sQuery(id+"F4.wireOp",EDGE,"E47"),sQuery(id+"F4.wireOp",EDGE,"E48"),sQuery(id+"F4.wireOp",EDGE,"E49"),sQuery(id+"F4.wireOp",EDGE,"E50"),sQuery(id+"F4.wireOp",EDGE,"E51"),sQuery(id+"F4.wireOp",EDGE,"E52"),sQuery(id+"F4.wireOp",EDGE,"E53"),sQuery(id+"F4.wireOp",EDGE,"E54"),sQuery(id+"F4.wireOp",EDGE,"E55"),sQuery(id+"F4.wireOp",EDGE,"E56"),sQuery(id+"F4.wireOp",EDGE,"E57"),sQuery(id+"F4.wireOp",EDGE,"E58"),sQuery(id+"F4.wireOp",EDGE,"E59"),sQuery(id+"F4.wireOp",EDGE,"E60")])],"isStart":true})]});
            var sketch = newSketch(context, id + "F8", { "sketchPlane" : qUnion([Q0])});
            skCircle(sketch, "E90", {"center": v(30.85, 17.33) * mm, "radius": 4.76 * mm});
            skPoint(sketch, "E90.centerSnap0", {"position": v(38.1, 17.33) * mm});
            skLineSegment(sketch, "E91", {"start": v(30.85, 30.17) * mm, "end": v(30.85, 4.34) * mm});
            skLineSegment(sketch, "E92", {"start": v(30.85, 30.17) * mm, "end": v(41.65, 30.17) * mm});
            skLineSegment(sketch, "E93", {"start": v(41.65, 30.17) * mm, "end": v(41.65, 4.34) * mm});
            skLineSegment(sketch, "E94", {"start": v(41.65, 4.34) * mm, "end": v(30.85, 4.34) * mm});
            skLineSegment(sketch, "E95", {"start": v(30.85, 17.33) * mm, "end": v(16.04, 4.9) * mm});
            skLineSegment(sketch, "E96", {"start": v(16.04, 4.9) * mm, "end": v(30.85, 4.9) * mm});
            skLineSegment(sketch, "E97", {"start": v(30.85, 4.34) * mm, "end": v(30.85, 4.9) * mm});
            skLineSegment(sketch, "E98", {"start": v(43.34, 12.57) * mm, "end": v(23.4, 12.57) * mm});
            skSolve(sketch);
        }
        {
            var Q0;
            {var subQ5=sQuery(id+"F8.wireOp",EDGE,"E92");Q0=makeQuery(id+"F8.imprint","IMPRINT",FACE,{"disambiguationData":[TD([[makeQuery(id+"F8.imprint","IMPRINT",EDGE,{"derivedFrom":subQ5}),-1.0]])]});}
            var Q1;
            {var subQ4=sQuery(id+"F0.wireOp",EDGE,"E31.right");var subQ7=makeQuery(id+"F1.opExtrude","CAP_EDGE",EDGE,{"disambiguationData":[OSD([subQ4])],"isStart":false});Q1=makeQuery(id+"F8.imprint","IMPRINT",FACE,{"disambiguationData":[TD([[makeQuery(id+"F8.imprint","IMPRINT",EDGE,{"derivedFrom":subQ7}),-1.0]])]});}
            var Q2;
            {var subQ0=sQuery(id+"F8.wireOp",EDGE,"E94");Q2=makeQuery(id+"F8.imprint","IMPRINT",FACE,{"disambiguationData":[TD([[makeQuery(id+"F8.imprint","IMPRINT",EDGE,{"derivedFrom":subQ0}),-1.0]])]});}
            var Q3;
            {var subQ0=sQuery(id+"F8.wireOp",EDGE,"E96");Q3=makeQuery(id+"F8.imprint","IMPRINT",FACE,{"disambiguationData":[TD([[makeQuery(id+"F8.imprint","IMPRINT",EDGE,{"derivedFrom":subQ0}),1.0]])]});}
            extrude(context, id + "F9", {"entities" : qUnion([Q0, Q1, Q2, Q3]), "operationType" : NewBodyOperationType.REMOVE, "oppositeDirection" : true, "depth" : 25.4 * mm});
        }
        {
            var Q0;
            Q0=makeQuery(id+"F9.boolean.opBoolean","MERGE",FACE,{"derivedFrom":[makeQuery(id+"F7.boolean.opBoolean","MERGE",FACE,{"derivedFrom":[makeQuery(id+"F1.opExtrude","SWEPT_FACE",FACE,{"disambiguationData":[OSD([sQuery(id+"F0.wireOp",EDGE,"E31.top")])]}),makeQuery(id+"F7.opExtrude","SWEPT_FACE",FACE,{"disambiguationData":[OSD([sQuery(id+"F6.wireOp",EDGE,"E80")])]})]}),makeQuery(id+"F9.opExtrude","SWEPT_FACE",FACE,{"disambiguationData":[OSD([sQuery(id+"F8.wireOp",EDGE,"E98")])]})]});
            var sketch = newSketch(context, id + "F10", { "sketchPlane" : qUnion([Q0])});
            skLineSegment(sketch, "E99.bottom", {"start": v(-32.5, 38.93) * mm, "end": v(-30.9, 38.93) * mm});
            skLineSegment(sketch, "E99.top", {"start": v(-32.5, 25.17) * mm, "end": v(-30.9, 25.17) * mm});
            skLineSegment(sketch, "E99.left", {"start": v(-32.5, 38.93) * mm, "end": v(-32.5, 25.17) * mm});
            skLineSegment(sketch, "E99.right", {"start": v(-30.9, 38.93) * mm, "end": v(-30.9, 25.17) * mm});
            skLineSegment(sketch, "E100.bottom", {"start": v(-30.9, 38.93) * mm, "end": v(-11.86, 38.93) * mm});
            skLineSegment(sketch, "E100.top", {"start": v(-30.9, 25.17) * mm, "end": v(-11.86, 25.17) * mm});
            skLineSegment(sketch, "E100.right", {"start": v(-11.86, 38.93) * mm, "end": v(-11.86, 25.17) * mm});
            skLineSegment(sketch, "E101.bottom", {"start": v(-11.86, 38.93) * mm, "end": v(-10.3, 38.93) * mm});
            skLineSegment(sketch, "E101.top", {"start": v(-11.86, 25.17) * mm, "end": v(-10.3, 25.17) * mm});
            skLineSegment(sketch, "E101.right", {"start": v(-10.3, 38.93) * mm, "end": v(-10.3, 25.17) * mm});
            skSolve(sketch);
        }
        {
            var Q0;
            {var subQ2=sQuery(id+"F10.wireOp",EDGE,"E100.bottom");Q0=makeQuery(id+"F10.imprint","IMPRINT",FACE,{"disambiguationData":[TD([[makeQuery(id+"F10.imprint","IMPRINT",EDGE,{"derivedFrom":subQ2}),-1.0]])]});}
            var Q1;
            {var subQ1=sQuery(id+"F8.wireOp",EDGE,"E98");var subQ2=makeQuery(id+"F9.opExtrude","SWEPT_FACE",FACE,{"disambiguationData":[OSD([subQ1])]});var subQ3=makeQuery(id+"F1.opExtrude","SWEPT_FACE",FACE,{"disambiguationData":[OSD([sQuery(id+"F0.wireOp",EDGE,"E0")])]});var subQ4=makeQuery(id+"F9.boolean.opBoolean","INTERSECT",EDGE,{"disambiguationData":[OD(1.0)],"derivedFrom":[subQ3,subQ2]});Q1=makeQuery(id+"F10.imprint","IMPRINT",FACE,{"disambiguationData":[TD([[makeQuery(id+"F10.imprint","IMPRINT",EDGE,{"derivedFrom":subQ4}),1.0]])]});}
            var Q2;
            Q2=makeQuery(id+"F7.boolean.opBoolean","MERGE",FACE,{"derivedFrom":[makeQuery(id+"F1.opExtrude","SWEPT_FACE",FACE,{"disambiguationData":[OSD([sQuery(id+"F0.wireOp",EDGE,"E30.bottom")])]}),makeQuery(id+"F7.opExtrude","SWEPT_FACE",FACE,{"disambiguationData":[OSD([sQuery(id+"F6.wireOp",EDGE,"E67")])]})]});
            extrude(context, id + "F11", {"entities" : qUnion([Q0, Q1]), "operationType" : NewBodyOperationType.REMOVE, "endBound" : BoundingType.UP_TO_SURFACE, "oppositeDirection" : true, "endBoundEntityFace" : qUnion([Q2]), "depth" : 25.4 * mm});
        }
        {
            var Q0;
            Q0=makeQuery(id+"F5.boolean.opBoolean","MERGE",FACE,{"derivedFrom":[makeQuery(id+"F1.opExtrude","SWEPT_FACE",FACE,{"disambiguationData":[OSD([sQuery(id+"F0.wireOp",EDGE,"E31.right")])]}),makeQuery(id+"F5.opExtrude","CAP_FACE",FACE,{"disambiguationData":[OSD([sQuery(id+"F4.wireOp",EDGE,"E46"),sQuery(id+"F4.wireOp",EDGE,"E47"),sQuery(id+"F4.wireOp",EDGE,"E48"),sQuery(id+"F4.wireOp",EDGE,"E49"),sQuery(id+"F4.wireOp",EDGE,"E50"),sQuery(id+"F4.wireOp",EDGE,"E51"),sQuery(id+"F4.wireOp",EDGE,"E52"),sQuery(id+"F4.wireOp",EDGE,"E53"),sQuery(id+"F4.wireOp",EDGE,"E54"),sQuery(id+"F4.wireOp",EDGE,"E55"),sQuery(id+"F4.wireOp",EDGE,"E56"),sQuery(id+"F4.wireOp",EDGE,"E57"),sQuery(id+"F4.wireOp",EDGE,"E58"),sQuery(id+"F4.wireOp",EDGE,"E59"),sQuery(id+"F4.wireOp",EDGE,"E60")])],"isStart":true})]});
            var sketch = newSketch(context, id + "F12", { "sketchPlane" : qUnion([Q0])});
            skCircle(sketch, "E102", {"center": v(30.85, 17.33) * mm, "radius": 4.76 * mm});
            skCircle(sketch, "E103", {"center": v(30.85, 17.33) * mm, "radius": 2.38 * mm});
            skSolve(sketch);
        }
        {
            var Q0;
            Q0=makeQuery(id+"F12.imprint","IMPRINT",FACE,{"disambiguationData":[TD([[makeQuery(id+"F12.imprint","IMPRINT",EDGE,{"derivedFrom":sQuery(id+"F12.wireOp",EDGE,"E103")}),1.0]])]});
            extrude(context, id + "F13", {"entities" : qUnion([Q0]), "operationType" : NewBodyOperationType.REMOVE, "oppositeDirection" : true, "depth" : 25.4 * mm});
        }
    });
